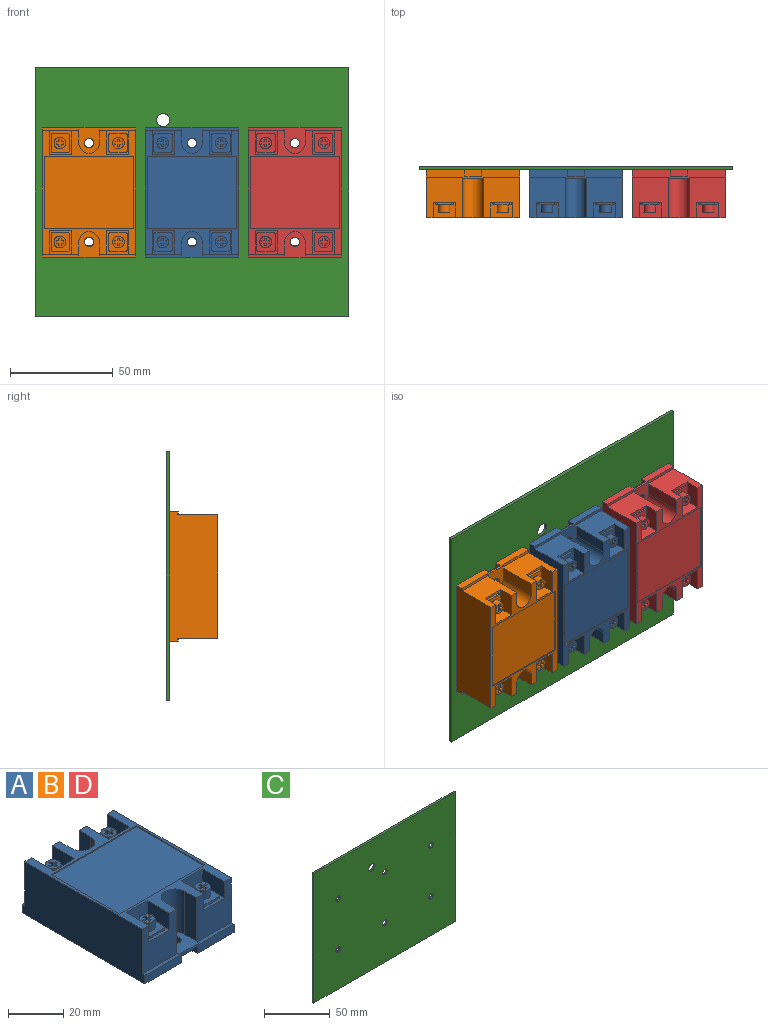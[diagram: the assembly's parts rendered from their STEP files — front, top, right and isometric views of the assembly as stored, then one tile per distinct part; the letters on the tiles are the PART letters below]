
ASSEMBLY  parts=4 mates=3
PART A: 153 faces, bbox 45.6x62.9x23.4 mm
  f0: plane 60x45.55mm, normal (0,0,1), area 518mm2, adj f5,f7,f8,f11,f12,f13,f20,f21
  f1: plane 62.88x45.55mm, normal (0,0,-1), area 2787.6mm2, adj f2,f6,f12,f13,f138,f139,f140,f142
  f2: plane 45.55x4.25mm, normal (0,-1,0), area 146.3mm2, adj f1,f4,f12,f13,f17,f18,f19,f137
  f3: plane 1.44x0.6mm, normal (-1,0,0), area 0.9mm2, adj f6,f8,f14,f132
  f4: plane 1.44x0.6mm, normal (-1,0,0), area 0.9mm2, adj f2,f11,f19,f137
  f5: plane 19.75x17.78mm, normal (0,-1,0), area 273.5mm2, adj f0,f9,f12,f17,f18,f27,f28,f134
  f6: plane 45.55x4.25mm, normal (0,1,0), area 146.3mm2, adj f1,f3,f12,f13,f14,f15,f16,f132
  f7: plane 19.75x17.78mm, normal (0,1,0), area 273.5mm2, adj f0,f12,f15,f16,f23,f25,f26,f130
  f8: plane 19.75x17.78mm, normal (0,1,0), area 273.5mm2, adj f0,f3,f10,f13,f14,f20,f22,f131
  f9: plane 11.5x10.7mm, normal (0,0,1), area 38.8mm2, adj f5,f27,f28,f29,f61,f62,f63,f64
  f10: plane 11.5x10.7mm, normal (0,0,1), area 38.8mm2, adj f8,f20,f21,f22,f34,f35,f36,f37
  f11: plane 19.75x17.78mm, normal (0,-1,0), area 273.5mm2, adj f0,f4,f13,f19,f30,f31,f33,f136
  f12: plane 62.88x23.4mm, normal (1,0,0), area 1414.5mm2, adj f0,f1,f2,f5,f6,f7,f16,f18
  f13: plane 62.88x23.4mm, normal (-1,0,0), area 1414.5mm2, adj f0,f1,f2,f6,f8,f11,f14,f19
  f14: plane 17.78x1.44mm, normal (0,0,1), area 25.6mm2, adj f3,f6,f8,f13
  f15: plane 1.44x0.6mm, normal (1,0,0), area 0.9mm2, adj f6,f7,f16,f132
  f16: plane 17.78x1.44mm, normal (0,0,1), area 25.6mm2, adj f6,f7,f12,f15
  f17: plane 1.44x0.6mm, normal (1,0,0), area 0.9mm2, adj f2,f5,f18,f137
  f18: plane 17.78x1.44mm, normal (0,0,1), area 25.6mm2, adj f2,f5,f12,f17
  f19: plane 17.78x1.44mm, normal (0,0,1), area 25.6mm2, adj f2,f4,f11,f13
  f20: plane 11.5x7.25mm, normal (1,0,0), area 83.4mm2, adj f0,f8,f10,f21
  f21: plane 10.7x7.25mm, normal (0,1,0), area 77.6mm2, adj f0,f10,f20,f22
  f22: plane 11.5x7.25mm, normal (-1,0,0), area 83.4mm2, adj f0,f8,f10,f21
  f23: plane 11.5x7.25mm, normal (1,0,0), area 83.4mm2, adj f0,f7,f24,f26
  f24: plane 10.7x7.25mm, normal (0,1,0), area 77.6mm2, adj f0,f23,f25,f26
  f25: plane 11.5x7.25mm, normal (-1,0,0), area 83.4mm2, adj f0,f7,f24,f26
  f26: plane 11.5x10.7mm, normal (0,0,1), area 38.8mm2, adj f7,f23,f24,f25,f43,f44,f45,f46
  f27: plane 11.5x7.25mm, normal (1,0,0), area 83.4mm2, adj f0,f5,f9,f29
  f28: plane 11.5x7.25mm, normal (-1,0,0), area 83.4mm2, adj f0,f5,f9,f29
  f29: plane 10.7x7.25mm, normal (0,-1,0), area 77.6mm2, adj f0,f9,f27,f28
  f30: plane 11.5x7.25mm, normal (1,0,0), area 83.4mm2, adj f0,f11,f32,f33
  f31: plane 11.5x7.25mm, normal (-1,0,0), area 83.4mm2, adj f0,f11,f32,f33
  f32: plane 10.7x7.25mm, normal (0,-1,0), area 77.6mm2, adj f0,f30,f31,f33
  f33: plane 11.5x10.7mm, normal (0,0,1), area 38.8mm2, adj f11,f30,f31,f32,f52,f53,f54,f55
  f34: plane 7.51x1mm, normal (1,0,0), area 7.5mm2, adj f10,f35,f41,f42
  f35: cylinder r=1mm len=1mm, axis (0,0,-1), area 1.6mm2, adj f10,f34,f36,f42
  f36: plane 6.95x1mm, normal (0,1,0), area 6.9mm2, adj f10,f35,f37,f42
  f37: cylinder r=1mm len=1mm, axis (0,0,-1), area 1.6mm2, adj f10,f36,f38,f42
  f38: plane 7.51x1mm, normal (-1,0,0), area 7.5mm2, adj f10,f37,f39,f42
  f39: cylinder r=1mm len=1mm, axis (0,0,-1), area 1.6mm2, adj f10,f38,f40,f42
  f40: plane 6.95x1mm, normal (0,-1,0), area 6.9mm2, adj f10,f39,f41,f42
  f41: cylinder r=1mm len=1mm, axis (0,0,-1), area 1.6mm2, adj f10,f34,f40,f42
  f42: plane 9.51x8.95mm, normal (0,0,1), area 59.1mm2, adj f34,f35,f36,f37,f38,f39,f40,f41
  f43: plane 7.51x1mm, normal (1,0,0), area 7.5mm2, adj f26,f44,f50,f51
  f44: cylinder r=1mm len=1mm, axis (0,0,-1), area 1.6mm2, adj f26,f43,f45,f51
  f45: plane 6.95x1mm, normal (0,1,0), area 6.9mm2, adj f26,f44,f46,f51
  f46: cylinder r=1mm len=1mm, axis (0,0,-1), area 1.6mm2, adj f26,f45,f47,f51
  f47: plane 7.51x1mm, normal (-1,0,0), area 7.5mm2, adj f26,f46,f48,f51
  f48: cylinder r=1mm len=1mm, axis (0,0,-1), area 1.6mm2, adj f26,f47,f49,f51
  f49: plane 6.95x1mm, normal (0,-1,0), area 6.9mm2, adj f26,f48,f50,f51
  f50: cylinder r=1mm len=1mm, axis (0,0,-1), area 1.6mm2, adj f26,f43,f49,f51
  f51: plane 9.51x8.95mm, normal (0,0,1), area 59.1mm2, adj f43,f44,f45,f46,f47,f48,f49,f50
  f52: cylinder r=1mm len=1mm, axis (0,0,-1), area 1.6mm2, adj f33,f53,f59,f60
  f53: plane 6.95x1mm, normal (0,-1,0), area 6.9mm2, adj f33,f52,f54,f60
  f54: cylinder r=1mm len=1mm, axis (0,0,-1), area 1.6mm2, adj f33,f53,f55,f60
  f55: plane 7.51x1mm, normal (1,0,0), area 7.5mm2, adj f33,f54,f56,f60
  f56: cylinder r=1mm len=1mm, axis (0,0,-1), area 1.6mm2, adj f33,f55,f57,f60
  f57: plane 6.95x1mm, normal (0,1,0), area 6.9mm2, adj f33,f56,f58,f60
  f58: cylinder r=1mm len=1mm, axis (0,0,-1), area 1.6mm2, adj f33,f57,f59,f60
  f59: plane 7.51x1mm, normal (-1,0,0), area 7.5mm2, adj f33,f52,f58,f60
  f60: plane 9.51x8.95mm, normal (0,0,1), area 59.1mm2, adj f52,f53,f54,f55,f56,f57,f58,f59
  f61: plane 6.95x1mm, normal (0,-1,0), area 6.9mm2, adj f9,f62,f68,f69
  f62: cylinder r=1mm len=1mm, axis (0,0,-1), area 1.6mm2, adj f9,f61,f63,f69
  f63: plane 7.51x1mm, normal (1,0,0), area 7.5mm2, adj f9,f62,f64,f69
  f64: cylinder r=1mm len=1mm, axis (0,0,-1), area 1.6mm2, adj f9,f63,f65,f69
  f65: plane 6.95x1mm, normal (0,1,0), area 6.9mm2, adj f9,f64,f66,f69
  f66: cylinder r=1mm len=1mm, axis (0,0,-1), area 1.6mm2, adj f9,f65,f67,f69
  f67: plane 7.51x1mm, normal (-1,0,0), area 7.5mm2, adj f9,f66,f68,f69
  f68: cylinder r=1mm len=1mm, axis (0,0,-1), area 1.6mm2, adj f9,f61,f67,f69
  f69: plane 9.51x8.95mm, normal (0,0,1), area 59.1mm2, adj f61,f62,f63,f64,f65,f66,f67,f68
  f70: plane 3.79x1.25mm, normal (-1,0,0), area 4.8mm2, adj f71,f82,f83,f84
  f71: plane 3.79x1.14mm, normal (0,1,0), area 4.3mm2, adj f70,f72,f83,f84
  f72: plane 3.79x1.25mm, normal (1,0,0), area 4.8mm2, adj f71,f73,f83,f84
  f73: plane 3.79x1.31mm, normal (0,1,0), area 5mm2, adj f72,f74,f83,f84
  f74: plane 3.79x1.03mm, normal (1,0,0), area 3.9mm2, adj f73,f75,f83,f84
  f75: plane 3.79x1.31mm, normal (0,-1,0), area 5mm2, adj f74,f76,f83,f84
  f76: plane 3.79x1.25mm, normal (1,0,0), area 4.8mm2, adj f75,f77,f83,f84
  f77: plane 3.79x1.14mm, normal (0,-1,0), area 4.3mm2, adj f76,f78,f83,f84
  f78: plane 3.79x1.25mm, normal (-1,0,0), area 4.8mm2, adj f77,f79,f83,f84
  f79: plane 3.79x1.31mm, normal (0,-1,0), area 5mm2, adj f78,f80,f83,f84
  f80: plane 3.79x1.03mm, normal (-1,0,0), area 3.9mm2, adj f79,f82,f83,f84
  f81: cylinder r=2.83mm len=5.66mm, axis (0,0,-1), area 67.4mm2, adj f42,f83
  f82: plane 3.79x1.31mm, normal (0,1,0), area 5mm2, adj f70,f80,f83,f84
  f83: plane 5.66x5.66mm, normal (0,0,1), area 18.5mm2, adj f70,f71,f72,f73,f74,f75,f76,f77
  f84: plane 3.76x3.53mm, normal (0,0,1), area 6.7mm2, adj f70,f71,f72,f73,f74,f75,f76,f77
  f85: plane 3.79x1.31mm, normal (0,1,0), area 5mm2, adj f86,f96,f98,f99
  f86: plane 3.79x1.25mm, normal (-1,0,0), area 4.8mm2, adj f85,f87,f98,f99
  f87: plane 3.79x1.14mm, normal (0,1,0), area 4.3mm2, adj f86,f88,f98,f99
  f88: plane 3.79x1.25mm, normal (1,0,0), area 4.8mm2, adj f87,f89,f98,f99
  f89: plane 3.79x1.31mm, normal (0,1,0), area 5mm2, adj f88,f90,f98,f99
  f90: plane 3.79x1.03mm, normal (1,0,0), area 3.9mm2, adj f89,f91,f98,f99
  f91: plane 3.79x1.31mm, normal (0,-1,0), area 5mm2, adj f90,f92,f98,f99
  f92: plane 3.79x1.25mm, normal (1,0,0), area 4.8mm2, adj f91,f93,f98,f99
  f93: plane 3.79x1.14mm, normal (0,-1,0), area 4.3mm2, adj f92,f94,f98,f99
  f94: plane 3.79x1.25mm, normal (-1,0,0), area 4.8mm2, adj f93,f95,f98,f99
  f95: plane 3.79x1.31mm, normal (0,-1,0), area 5mm2, adj f94,f96,f98,f99
  f96: plane 3.79x1.03mm, normal (-1,0,0), area 3.9mm2, adj f85,f95,f98,f99
  f97: cylinder r=2.83mm len=5.66mm, axis (0,0,-1), area 67.4mm2, adj f51,f98
  f98: plane 5.66x5.66mm, normal (0,0,1), area 18.5mm2, adj f85,f86,f87,f88,f89,f90,f91,f92
  f99: plane 3.76x3.53mm, normal (0,0,1), area 6.7mm2, adj f85,f86,f87,f88,f89,f90,f91,f92
  f100: plane 3.79x1.31mm, normal (0,-1,0), area 5mm2, adj f101,f111,f113,f114
  f101: plane 3.79x1.03mm, normal (-1,0,0), area 3.9mm2, adj f100,f102,f113,f114
  f102: plane 3.79x1.31mm, normal (0,1,0), area 5mm2, adj f101,f103,f113,f114
  f103: plane 3.79x1.25mm, normal (-1,0,0), area 4.8mm2, adj f102,f104,f113,f114
  f104: plane 3.79x1.14mm, normal (0,1,0), area 4.3mm2, adj f103,f105,f113,f114
  f105: plane 3.79x1.25mm, normal (1,0,0), area 4.8mm2, adj f104,f106,f113,f114
  f106: plane 3.79x1.31mm, normal (0,1,0), area 5mm2, adj f105,f107,f113,f114
  f107: plane 3.79x1.03mm, normal (1,0,0), area 3.9mm2, adj f106,f108,f113,f114
  f108: plane 3.79x1.31mm, normal (0,-1,0), area 5mm2, adj f107,f109,f113,f114
  f109: plane 3.79x1.25mm, normal (1,0,0), area 4.8mm2, adj f108,f110,f113,f114
  f110: plane 3.79x1.14mm, normal (0,-1,0), area 4.3mm2, adj f109,f111,f113,f114
  f111: plane 3.79x1.25mm, normal (-1,0,0), area 4.8mm2, adj f100,f110,f113,f114
  f112: cylinder r=2.83mm len=5.66mm, axis (0,0,-1), area 67.4mm2, adj f60,f113
  f113: plane 5.66x5.66mm, normal (0,0,1), area 18.5mm2, adj f100,f101,f102,f103,f104,f105,f106,f107
  f114: plane 3.76x3.53mm, normal (0,0,1), area 6.7mm2, adj f100,f101,f102,f103,f104,f105,f106,f107
  f115: plane 3.79x1.31mm, normal (0,1,0), area 5mm2, adj f116,f126,f128,f129
  f116: plane 3.79x1.03mm, normal (1,0,0), area 3.9mm2, adj f115,f117,f128,f129
  f117: plane 3.79x1.31mm, normal (0,-1,0), area 5mm2, adj f116,f118,f128,f129
  f118: plane 3.79x1.25mm, normal (1,0,0), area 4.8mm2, adj f117,f119,f128,f129
  f119: plane 3.79x1.14mm, normal (0,-1,0), area 4.3mm2, adj f118,f120,f128,f129
  f120: plane 3.79x1.25mm, normal (-1,0,0), area 4.8mm2, adj f119,f121,f128,f129
  f121: plane 3.79x1.31mm, normal (0,-1,0), area 5mm2, adj f120,f122,f128,f129
  f122: plane 3.79x1.03mm, normal (-1,0,0), area 3.9mm2, adj f121,f123,f128,f129
  f123: plane 3.79x1.31mm, normal (0,1,0), area 5mm2, adj f122,f124,f128,f129
  f124: plane 3.79x1.25mm, normal (-1,0,0), area 4.8mm2, adj f123,f125,f128,f129
  f125: plane 3.79x1.14mm, normal (0,1,0), area 4.3mm2, adj f124,f126,f128,f129
  f126: plane 3.79x1.25mm, normal (1,0,0), area 4.8mm2, adj f115,f125,f128,f129
  f127: cylinder r=2.83mm len=5.66mm, axis (0,0,-1), area 67.4mm2, adj f69,f128
  f128: plane 5.66x5.66mm, normal (0,0,1), area 18.5mm2, adj f115,f116,f117,f118,f119,f120,f121,f122
  f129: plane 3.76x3.53mm, normal (0,0,1), area 6.7mm2, adj f115,f116,f117,f118,f119,f120,f121,f122
  f130: plane 19.15x6mm, normal (-1,0,0), area 114.9mm2, adj f0,f7,f132,f133
  f131: plane 19.15x6mm, normal (1,0,0), area 114.9mm2, adj f0,f8,f132,f133
  f132: plane 12.44x10mm, normal (0,0,1), area 97.8mm2, adj f3,f6,f15,f130,f131,f133,f147
  f133: cylinder r=5mm len=19.15mm, axis (0,0,1), area 300.8mm2, adj f0,f130,f131,f132
  f134: plane 19.15x6mm, normal (-1,0,0), area 114.9mm2, adj f0,f5,f135,f137
  f135: cylinder r=5mm len=19.15mm, axis (0,0,1), area 300.8mm2, adj f0,f134,f136,f137
  f136: plane 19.15x6mm, normal (1,0,0), area 114.9mm2, adj f0,f11,f135,f137
  f137: plane 12.44x10mm, normal (0,0,1), area 97.8mm2, adj f2,f4,f17,f134,f135,f136,f146
  f138: plane 3.25x2.8mm, normal (-1,0,0), area 9.1mm2, adj f1,f6,f139,f141
  f139: plane 8x3.25mm, normal (0,1,0), area 26mm2, adj f1,f138,f140,f141
  f140: plane 3.25x2.8mm, normal (1,0,0), area 9.1mm2, adj f1,f6,f139,f141
  f141: plane 8x2.8mm, normal (0,0,-1), area 22.4mm2, adj f6,f138,f139,f140
  f142: plane 3.25x2.8mm, normal (-1,0,0), area 9.1mm2, adj f1,f2,f144,f145
  f143: plane 3.25x2.8mm, normal (1,0,0), area 9.1mm2, adj f1,f2,f144,f145
  f144: plane 8x3.25mm, normal (0,-1,0), area 26mm2, adj f1,f142,f143,f145
  f145: plane 8x2.8mm, normal (0,0,-1), area 22.4mm2, adj f2,f142,f143,f144
  f146: cylinder r=2.25mm len=4.5mm, axis (0,0,1), area 60.1mm2, adj f1,f137
  f147: cylinder r=2.25mm len=4.5mm, axis (0,0,1), area 60.1mm2, adj f1,f132
  f148: plane 43.55x0.5mm, normal (0,1,0), area 21.8mm2, adj f0,f149,f151,f152
  f149: plane 35x0.5mm, normal (-1,0,0), area 17.5mm2, adj f0,f148,f150,f152
  f150: plane 43.55x0.5mm, normal (0,-1,0), area 21.8mm2, adj f0,f149,f151,f152
  f151: plane 35x0.5mm, normal (1,0,0), area 17.5mm2, adj f0,f148,f150,f152
  f152: plane 43.55x35mm, normal (0,0,1), area 1524.2mm2, adj f148,f149,f150,f151
PART B: same geometry as A
PART C: 13 faces, bbox 152.4x1.6x120.7 mm
  f0: plane 120.65x1.59mm, normal (1,0,0), area 191.5mm2, adj f1,f3,f4,f5
  f1: plane 152.4x1.59mm, normal (0,0,1), area 241.9mm2, adj f0,f2,f4,f5
  f2: plane 120.65x1.59mm, normal (-1,0,0), area 191.5mm2, adj f1,f3,f4,f5
  f3: plane 152.4x1.59mm, normal (0,0,-1), area 241.9mm2, adj f0,f2,f4,f5
  f4: plane 152.4x120.65mm, normal (0,-1,0), area 18237.6mm2, adj f0,f1,f2,f3,f6,f7,f8,f9
  f5: plane 152.4x120.65mm, normal (0,1,0), area 18237.6mm2, adj f0,f1,f2,f3,f6,f7,f8,f9
  f6: cylinder r=2.5mm len=5mm, axis (0,-1,0), area 24.9mm2, adj f4,f5
  f7: cylinder r=2.5mm len=5mm, axis (0,-1,0), area 24.9mm2, adj f4,f5
  f8: cylinder r=2.5mm len=5mm, axis (0,-1,0), area 24.9mm2, adj f4,f5
  f9: cylinder r=2.5mm len=5mm, axis (0,-1,0), area 24.9mm2, adj f4,f5
  f10: cylinder r=2.5mm len=5mm, axis (0,-1,0), area 24.9mm2, adj f4,f5
  f11: cylinder r=2.5mm len=5mm, axis (0,-1,0), area 24.9mm2, adj f4,f5
  f12: cylinder r=3.17mm len=6.35mm, axis (0,-1,0), area 31.7mm2, adj f4,f5
PART D: same geometry as A
PLACE A rot(axis=(1,0,0),90deg) t=(-0.29,-0.64,0.23)mm
PLACE B rot(axis=(1,0,0),90deg) t=(-50.29,-0.64,0.23)mm
PLACE C t=(-0.29,0.95,0.48)mm
PLACE D rot(axis=(1,0,0),90deg) t=(49.71,-0.64,0.23)mm
MATE fastened B.f147 <-> C.f6  axis (0,1,0) through (-50.29,-0.64,24.23)mm
MATE fastened A.f147 <-> C.f7  axis (0,1,0) through (-0.29,-0.64,24.23)mm
MATE fastened D.f147 <-> C.f8  axis (0,1,0) through (49.71,-0.64,24.23)mm
